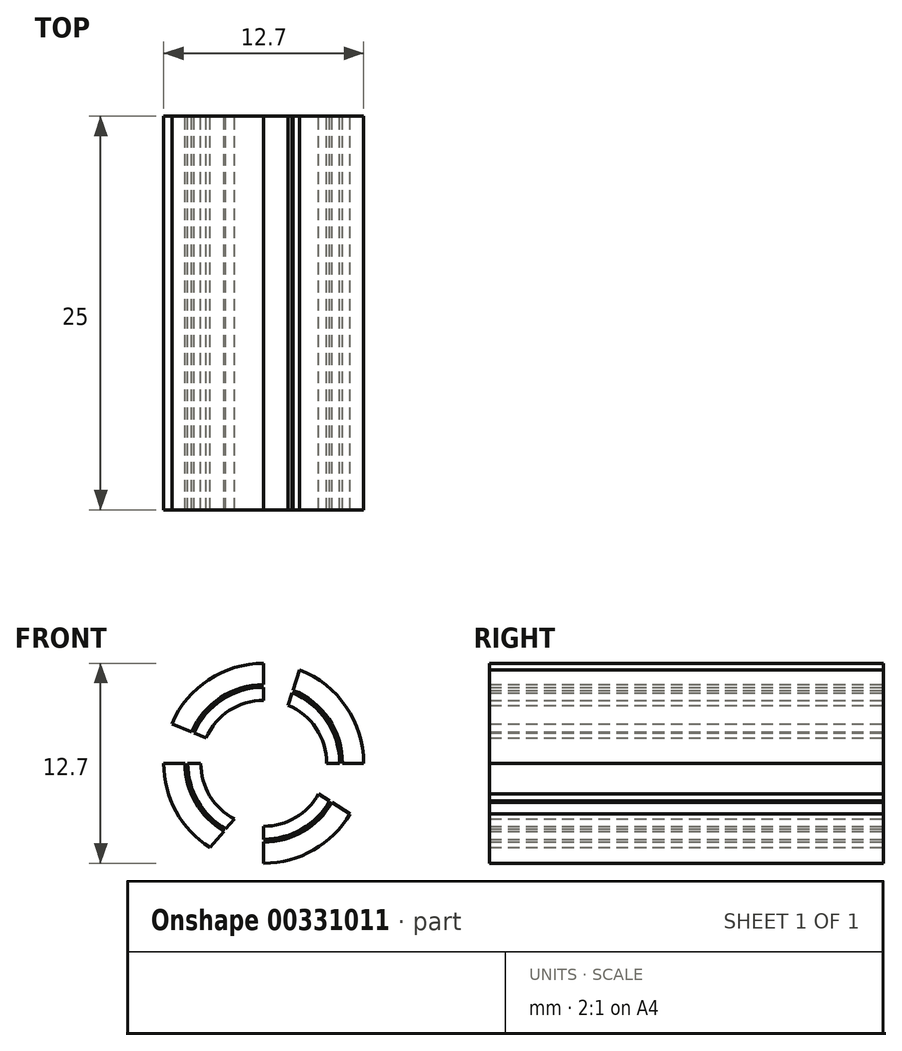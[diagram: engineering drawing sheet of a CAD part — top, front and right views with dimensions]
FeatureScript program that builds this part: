
annotation { "Feature Type Name" : "Feature", "Feature Type Description" : "" }
export const myFeature = defineFeature(function(context is Context, id is Id, definition is map)
    precondition{}
    {
        {
            var Q0;
            Q0=qCreatedBy(makeId("Front.planeOp"),FACE);
            var sketch = newSketch(context, id + "F0", { "sketchPlane" : qUnion([Q0])});
            skCircle(sketch, "E0", {"center": v(0, 0) * mm, "radius": 4 * mm});
            skCircle(sketch, "E1", {"center": v(0, 0) * mm, "radius": 6.35 * mm});
            skLineSegment(sketch, "E2", {"start": v(0, 4) * mm, "end": v(0, 6.35) * mm});
            skLineSegment(sketch, "E3", {"start": v(2.28, 5.93) * mm, "end": v(1.54, 3.7) * mm});
            skLineSegment(sketch, "E4", {"start": v(4, 0) * mm, "end": v(6.35, 0) * mm});
            skLineSegment(sketch, "E5", {"start": v(5.48, -3.2) * mm, "end": v(3.5, -1.95) * mm});
            skLineSegment(sketch, "E6", {"start": v(0, -4) * mm, "end": v(0, -6.35) * mm});
            skLineSegment(sketch, "E7", {"start": v(-3.42, -5.35) * mm, "end": v(-1.86, -3.54) * mm});
            skLineSegment(sketch, "E8", {"start": v(-4, 0) * mm, "end": v(-6.35, 0) * mm});
            skLineSegment(sketch, "E9", {"start": v(-5.83, 2.5) * mm, "end": v(-3.66, 1.6) * mm});
            skCircle(sketch, "E10", {"center": v(0, 0) * mm, "radius": 5 * mm});
            skCircle(sketch, "E11", {"center": v(0, 0) * mm, "radius": 4.83 * mm});
            skSolve(sketch);
        }
        {
            var Q0;
            {var subQ0=sQuery(id+"F0.wireOp",EDGE,"E5");var subQ1=sQuery(id+"F0.wireOp",EDGE,"E1");var subQ2=makeQuery(id+"F0.imprint","INTERSECT",VERTEX,{"derivedFrom":[subQ1,subQ0]});Q0=makeQuery(id+"F0.imprint","IMPRINT",FACE,{"disambiguationData":[TD([[makeQuery(id+"F0.imprint","IMPRINT",EDGE,{"disambiguationData":[TD([[subQ2,1.0]])],"derivedFrom":subQ1}),1.0]])]});}
            var Q1;
            {var subQ0=sQuery(id+"F0.wireOp",EDGE,"E7");var subQ1=sQuery(id+"F0.wireOp",EDGE,"E1");var subQ2=makeQuery(id+"F0.imprint","INTERSECT",VERTEX,{"derivedFrom":[subQ1,subQ0]});Q1=makeQuery(id+"F0.imprint","IMPRINT",FACE,{"disambiguationData":[TD([[makeQuery(id+"F0.imprint","IMPRINT",EDGE,{"disambiguationData":[TD([[subQ2,1.0]])],"derivedFrom":subQ1}),1.0]])]});}
            var Q2;
            {var subQ0=sQuery(id+"F0.wireOp",EDGE,"E2");var subQ1=sQuery(id+"F0.wireOp",EDGE,"E1");var subQ2=makeQuery(id+"F0.imprint","INTERSECT",VERTEX,{"derivedFrom":[subQ1,subQ0]});Q2=makeQuery(id+"F0.imprint","IMPRINT",FACE,{"disambiguationData":[TD([[makeQuery(id+"F0.imprint","IMPRINT",EDGE,{"disambiguationData":[TD([[subQ2,-1.0]])],"derivedFrom":subQ1}),1.0]])]});}
            var Q3;
            {var subQ0=sQuery(id+"F0.wireOp",EDGE,"E3");var subQ1=sQuery(id+"F0.wireOp",EDGE,"E1");var subQ2=makeQuery(id+"F0.imprint","INTERSECT",VERTEX,{"derivedFrom":[subQ1,subQ0]});Q3=makeQuery(id+"F0.imprint","IMPRINT",FACE,{"disambiguationData":[TD([[makeQuery(id+"F0.imprint","IMPRINT",EDGE,{"disambiguationData":[TD([[subQ2,1.0]])],"derivedFrom":subQ1}),1.0]])]});}
            var Q4;
            {var subQ0=sQuery(id+"F0.wireOp",EDGE,"E3");var subQ1=sQuery(id+"F0.wireOp",EDGE,"E0");var subQ2=makeQuery(id+"F0.imprint","INTERSECT",VERTEX,{"derivedFrom":[subQ1,subQ0]});Q4=makeQuery(id+"F0.imprint","IMPRINT",FACE,{"disambiguationData":[TD([[makeQuery(id+"F0.imprint","IMPRINT",EDGE,{"disambiguationData":[TD([[subQ2,1.0]])],"derivedFrom":subQ1}),-1.0]])]});}
            var Q5;
            {var subQ0=sQuery(id+"F0.wireOp",EDGE,"E2");var subQ1=sQuery(id+"F0.wireOp",EDGE,"E0");var subQ2=makeQuery(id+"F0.imprint","INTERSECT",VERTEX,{"derivedFrom":[subQ1,subQ0]});Q5=makeQuery(id+"F0.imprint","IMPRINT",FACE,{"disambiguationData":[TD([[makeQuery(id+"F0.imprint","IMPRINT",EDGE,{"disambiguationData":[TD([[subQ2,-1.0]])],"derivedFrom":subQ1}),-1.0]])]});}
            var Q6;
            {var subQ0=sQuery(id+"F0.wireOp",EDGE,"E7");var subQ1=sQuery(id+"F0.wireOp",EDGE,"E0");var subQ2=makeQuery(id+"F0.imprint","INTERSECT",VERTEX,{"derivedFrom":[subQ1,subQ0]});Q6=makeQuery(id+"F0.imprint","IMPRINT",FACE,{"disambiguationData":[TD([[makeQuery(id+"F0.imprint","IMPRINT",EDGE,{"disambiguationData":[TD([[subQ2,1.0]])],"derivedFrom":subQ1}),-1.0]])]});}
            var Q7;
            {var subQ0=sQuery(id+"F0.wireOp",EDGE,"E5");var subQ1=sQuery(id+"F0.wireOp",EDGE,"E0");var subQ2=makeQuery(id+"F0.imprint","INTERSECT",VERTEX,{"derivedFrom":[subQ1,subQ0]});Q7=makeQuery(id+"F0.imprint","IMPRINT",FACE,{"disambiguationData":[TD([[makeQuery(id+"F0.imprint","IMPRINT",EDGE,{"disambiguationData":[TD([[subQ2,1.0]])],"derivedFrom":subQ1}),-1.0]])]});}
            extrude(context, id + "F1", {"entities" : qUnion([Q0, Q1, Q2, Q3, Q4, Q5, Q6, Q7]), "depth" : 25 * mm});
        }
    });
